# Revit family: Sanitary_Taps-Mixers_hansgrohe_73445CHN-Tecturis-E-Single-lever-bath-mi__
name_source: partatom
category: Plumbing Fixtures
revit_build: Autodesk Revit 2018 (Build: 20170223_1515(x64)
units: mm (PartAtom-declared; Revit-internal decimal feet)

## family parameters
Always vertical = No
Cut with Voids When Loaded = No
OmniClass Number = 23.31.11.00
OmniClass Title = Faucets
Part Type = Normal
Room Calculation Point = No
Round Connector Dimension = Use Diameter
Shared = No
Work Plane-Based = Yes

## types (4) — shared parameters
Always visible = Yes
BIMobject category = Taps & Mixers
Default Elevation = 1219.2 mm  [stored 4 ft]
Description = Tecturis E Single lever bath mixer floor-standing
Design country = Germany
Edition number = 1
IFC Classification = Valve
Manufacturer = Hansgrohe
Manufacturer country = Germany
Manufacturer name = hansgrohe
Masterformat 2014 Code = 22 41 39
Masterformat 2014 Description = Residential Faucets, Supplies, and Trim
Model = 73445CHN
OmniClass Code = 23-31 11 00
OmniClass Description = Faucets
Product Guid = 11e3aa07-4cd2-4d11-9b49-1a277cba49e3
Product SKU = 73445CHN
Product data url = https://bimobject.com
Product family = Tecturis E
Product group = Bath mixers
Product name = 73445CHN Tecturis E Single lever bath mixer floor-standing
Product url = https://pro.hansgrohe.com
QR code = https://bimobject.com
UNSPSC Code = 3018
URL = https://www.hansgrohe.com
Uniclass 2015 Code = Pr_40_20_87
Uniclass 2015 Name = Taps and water supply outlet fittings
Uniformat II Code = D2010
Uniformat II Description = Plumbing Fixtures

## per-type parameters (varying)
| type | Material 1 |
| 700 Matte White | Hansgrohe - Metal - 707 Matte White |
| 670 Matte Black | Hansgrohe - Metal - 677 Matte Black |
| 140 Brushed Bronze | Hansgrohe - Metal - 147 Brushed Bronze |
| 000 Chrome | Hansgrohe - Metal - 007 Chrome |

note: [stored X ft] marks values corroborated as IEEE doubles in the binary element streams (Revit-internal decimal feet)

## geometry (parser evidence)
native form markers: Sweep x3
no freeform markers — native parametric forms only
